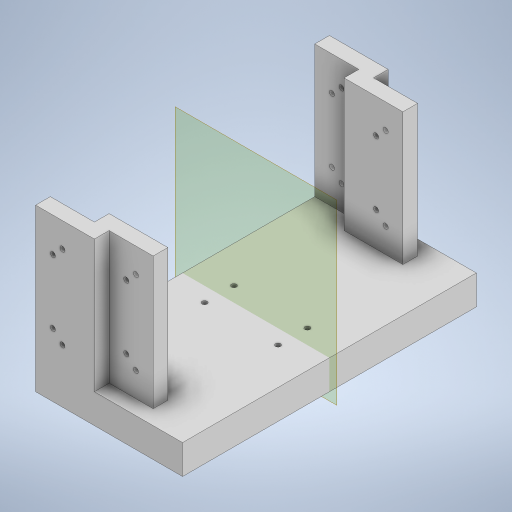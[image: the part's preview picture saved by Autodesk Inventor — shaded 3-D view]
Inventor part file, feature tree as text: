
AUTODESK INVENTOR PART (.ipt)
format: ipt  version: 2023 (Build 270158000, 158)  size: 346,624 bytes
history: native  units: mm
features: sketch x7, extrude x4, hole x3, other x1, mirror x1, plane x1
ambient origin geometry x8: Origin, YZ Plane, XZ Plane, XY Plane, X Axis, Y Axis, Z Axis, Center Point
bodies: Body1 (feature_tree)
feature tree (17):
  other  "Sólido1"
  extrude  "Extrusión1"  Depth=90.0mm
  hole  "Agujero1"  [1 undecoded]
  extrude  "Extrusión2"  TaperAngle=0.0deg  [1 undecoded]
  extrude  "Extrusión3"  Depth=90.0mm
  hole  "Agujero2"  [1 undecoded]
  extrude  "Extrusión4"  Depth=10.0mm TaperAngle=0.0deg
  mirror  "Simetría1"
  plane  "Plano de trabajo2"
  hole  "Agujero3"  [1 undecoded]
  sketch  "Boceto1"  dims[d0=30.0mm d1=90.0mm]
  sketch  "Boceto2"  dims[d2=10.0mm d3=0.0mm]
  sketch  "Boceto3"  dims[d4=1.75mm d5=1.75mm d6=1.75mm d7=1.75mm d8=10.0mm d9=10.0mm d10=10.0mm d11=15.0mm d12=0.0mm]
  sketch  "Boceto4"  dims[d13=30.0mm d14=0.0mm]
  sketch  "Boceto5"  dims[d15=90.0mm d16=15.0mm]
  sketch  "Boceto6"  dims[d17=3.5mm d18=6.0mm d19=4.0mm d20=2.0mm d21=90.0deg d22=8.0mm d23=20.594885mm d24=20.0mm]
  sketch  "Boceto7"  dims[d25=90.0mm d26=10.0mm d27=0.0mm d28=30.0mm d29=0.0mm d30=3.5mm d31=1.75mm d32=1.75mm d33=1.75mm d34=1.75mm d35=10.0mm d36=10.0mm d38=10.0mm d39=-41.10961mm d40=15.0mm d41=0.0mm d42=15.0mm d43=90.0mm d45=0.0mm d46=3.5mm d47=6.0mm d48=4.0mm d49=2.0mm d50=90.0deg d51=8.0mm d52=20.594885mm d53=20.0mm d54=100.0mm d55=0.0mm d56=5.0mm d57=5.0mm d58=3.5mm d59=5.0mm d60=5.0mm d61=10.0mm d62=30.0mm d64=20.0mm d65=3.5mm d66=6.0mm d67=4.0mm d68=2.0mm d69=90.0deg d70=8.0mm d71=20.594885mm]
note: 4 required parameter values undecoded (feature->parameter linkage not recoverable at this tier; creation-order binding heuristic only, values carry confidence <= 0.55)
